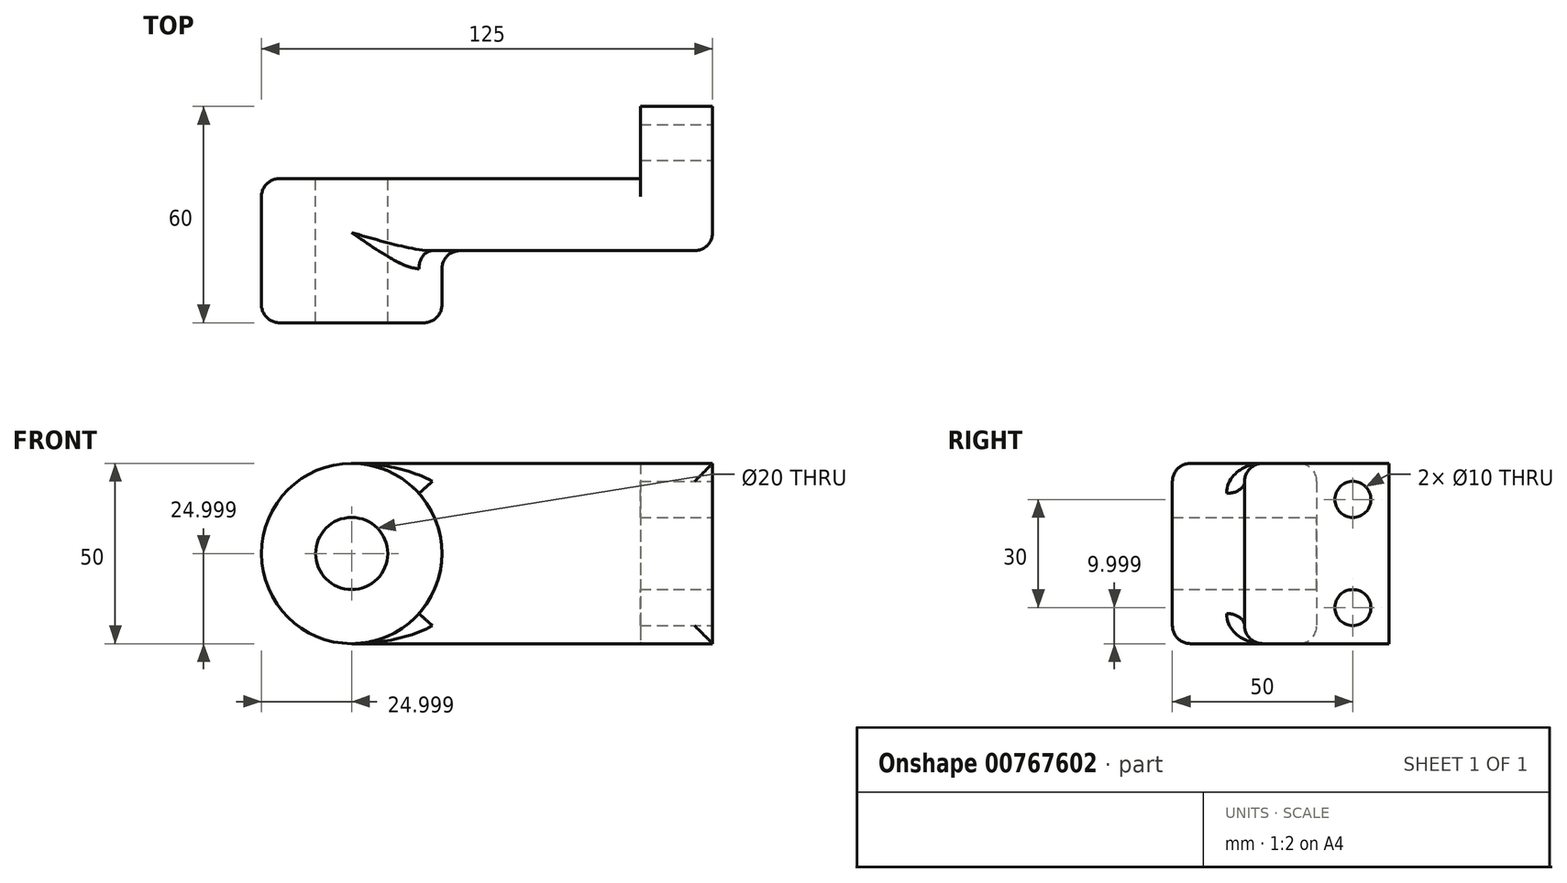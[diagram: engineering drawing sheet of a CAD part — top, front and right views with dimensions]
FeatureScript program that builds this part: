
annotation { "Feature Type Name" : "Feature", "Feature Type Description" : "" }
export const myFeature = defineFeature(function(context is Context, id is Id, definition is map)
    precondition{}
    {
        {
            var Q0;
            Q0=qCreatedBy(makeId("Front.planeOp"),FACE);
            var sketch = newSketch(context, id + "F0", { "sketchPlane" : qUnion([Q0])});
            skLineSegment(sketch, "E0.bottom", {"start": v(-62.77, 23.54) * mm, "end": v(37.23, 23.54) * mm});
            skLineSegment(sketch, "E0.top", {"start": v(-62.77, -26.46) * mm, "end": v(37.23, -26.46) * mm});
            skLineSegment(sketch, "E0.left", {"start": v(-62.77, 23.54) * mm, "end": v(-62.77, -26.46) * mm});
            skLineSegment(sketch, "E0.right", {"start": v(37.23, 23.54) * mm, "end": v(37.23, -26.46) * mm});
            skSolve(sketch);
        }
        {
            var Q0;
            Q0=qCreatedBy(makeId("Front.planeOp"),FACE);
            var sketch = newSketch(context, id + "F1", { "sketchPlane" : qUnion([Q0])});
            skCircle(sketch, "E1", {"center": v(-62.77, -1.46) * mm, "radius": 25 * mm});
            skCircle(sketch, "E2", {"center": v(-62.77, -1.46) * mm, "radius": 10 * mm});
            skSolve(sketch);
        }
        {
            var Q0;
            Q0=makeQuery(id+"F0.imprint","IMPRINT",FACE,{"disambiguationData":[TD([[makeQuery(id+"F0.imprint","IMPRINT",EDGE,{"derivedFrom":sQuery(id+"F0.wireOp",EDGE,"E0.bottom")}),-1.0]])]});
            extrude(context, id + "F2", {"entities" : qUnion([Q0]), "depth" : 20 * mm, "offsetDistance" : 25 * mm});
        }
        {
            var Q0;
            Q0=makeQuery(id+"F1.imprint","IMPRINT",FACE,{"disambiguationData":[TD([[makeQuery(id+"F1.imprint","IMPRINT",EDGE,{"derivedFrom":sQuery(id+"F1.wireOp",EDGE,"E1")}),1.0]])]});
            extrude(context, id + "F3", {"entities" : qUnion([Q0]), "operationType" : NewBodyOperationType.ADD, "depth" : 40 * mm, "offsetDistance" : 25 * mm});
        }
        {
            var Q0;
            {var subQ0=sQuery(id+"F0.wireOp",EDGE,"E0.left");Q0=makeQuery(id+"F3.boolean.opBoolean","SPLIT",FACE,{"disambiguationData":[TD([makeQuery(id+"F2.opExtrude","SWEPT_FACE",FACE,{"disambiguationData":[OSD([subQ0])]})])],"derivedFrom":makeQuery(id+"F2.opExtrude","CAP_FACE",FACE,{"disambiguationData":[OSD([sQuery(id+"F0.wireOp",EDGE,"E0.bottom"),sQuery(id+"F0.wireOp",EDGE,"E0.top"),subQ0,sQuery(id+"F0.wireOp",EDGE,"E0.right")])],"isStart":false})});}
            extrude(context, id + "F4", {"entities" : qUnion([Q0]), "operationType" : NewBodyOperationType.REMOVE, "oppositeDirection" : true, "depth" : 25 * mm, "offsetDistance" : 25 * mm});
        }
        {
            var Q0;
            Q0=qCreatedBy(makeId("Front.planeOp"),FACE);
            var sketch = newSketch(context, id + "F5", { "sketchPlane" : qUnion([Q0])});
            skLineSegment(sketch, "E3.bottom", {"start": v(17.23, 23.54) * mm, "end": v(37.23, 23.54) * mm});
            skLineSegment(sketch, "E3.top", {"start": v(17.23, -26.46) * mm, "end": v(37.23, -26.46) * mm});
            skLineSegment(sketch, "E3.left", {"start": v(17.23, 23.54) * mm, "end": v(17.23, -26.46) * mm});
            skLineSegment(sketch, "E3.right", {"start": v(37.23, 23.54) * mm, "end": v(37.23, -26.46) * mm});
            skSolve(sketch);
        }
        {
            var Q0;
            Q0=makeQuery(id+"F5.imprint","IMPRINT",FACE,{"disambiguationData":[TD([[makeQuery(id+"F5.imprint","IMPRINT",EDGE,{"derivedFrom":sQuery(id+"F5.wireOp",EDGE,"E3.bottom")}),-1.0]])]});
            extrude(context, id + "F6", {"entities" : qUnion([Q0]), "operationType" : NewBodyOperationType.ADD, "oppositeDirection" : true, "depth" : 20 * mm, "offsetDistance" : 25 * mm});
        }
        {
            var Q0;
            Q0=makeQuery(id+"F6.boolean.opBoolean","MERGE",FACE,{"derivedFrom":[makeQuery(id+"F2.opExtrude","SWEPT_FACE",FACE,{"disambiguationData":[OSD([sQuery(id+"F0.wireOp",EDGE,"E0.right")])]}),makeQuery(id+"F6.opExtrude","SWEPT_FACE",FACE,{"disambiguationData":[OSD([sQuery(id+"F5.wireOp",EDGE,"E3.right")])]})]});
            var sketch = newSketch(context, id + "F7", { "sketchPlane" : qUnion([Q0])});
            skCircle(sketch, "E4", {"center": v(10, -16.46) * mm, "radius": 5 * mm});
            skCircle(sketch, "E5", {"center": v(10, 13.54) * mm, "radius": 5 * mm});
            skSolve(sketch);
        }
        {
            var Q0;
            Q0=makeQuery(id+"F7.imprint","IMPRINT",FACE,{"disambiguationData":[TD([[makeQuery(id+"F7.imprint","IMPRINT",EDGE,{"derivedFrom":sQuery(id+"F7.wireOp",EDGE,"E4")}),1.0]])]});
            var Q1;
            Q1=makeQuery(id+"F7.imprint","IMPRINT",FACE,{"disambiguationData":[TD([[makeQuery(id+"F7.imprint","IMPRINT",EDGE,{"derivedFrom":sQuery(id+"F7.wireOp",EDGE,"E5")}),1.0]])]});
            extrude(context, id + "F8", {"entities" : qUnion([Q0, Q1]), "operationType" : NewBodyOperationType.REMOVE, "oppositeDirection" : true, "depth" : 20 * mm, "offsetDistance" : 25 * mm});
        }
        {
            var Q0;
            Q0=makeQuery(id+"F3.opExtrude","SWEPT_FACE",FACE,{"disambiguationData":[OSD([sQuery(id+"F1.wireOp",EDGE,"E1")])]});
            var Q1;
            {var subQ0=sQuery(id+"F0.wireOp",EDGE,"E0.bottom");var subQ1=sQuery(id+"F0.wireOp",EDGE,"E0.right");var subQ2=sQuery(id+"F0.wireOp",EDGE,"E0.top");Q1=makeQuery(id+"F3.boolean.opBoolean","SPLIT",FACE,{"disambiguationData":[TD([makeQuery(id+"F2.opExtrude","SWEPT_FACE",FACE,{"disambiguationData":[OSD([subQ0])]})])],"derivedFrom":makeQuery(id+"F2.opExtrude","CAP_FACE",FACE,{"disambiguationData":[OSD([subQ0,subQ2,sQuery(id+"F0.wireOp",EDGE,"E0.left"),subQ1])],"isStart":false})});}
            fillet(context, id + "F9", {"entities" : qUnion([Q0, Q1]), "radius" : 5 * mm, "tangentPropagation" : true, "allowEdgeOverflow" : false});
        }
    });
